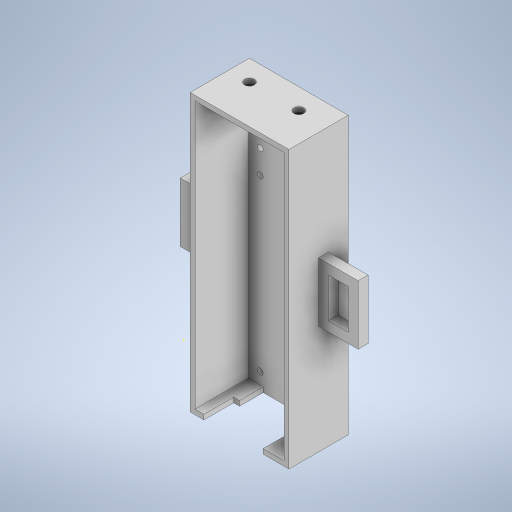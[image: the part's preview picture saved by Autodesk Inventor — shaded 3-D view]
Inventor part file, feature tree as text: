
AUTODESK INVENTOR PART (.ipt)
format: ipt  version: 2023 (Build 270158000, 158)  size: 340,480 bytes
history: native  units: mm
features: sketch x7, extrude x6, plane x1
ambient origin geometry x8: Origin, YZ Plane, XZ Plane, XY Plane, X Axis, Y Axis, Z Axis, Center Point
bodies: Solid1 (feature_tree)
feature tree (14):
  extrude  "Extrusion1"  Depth=50.0mm
  extrude  "Extrusion2"  Depth=2.5mm
  extrude  "Extrusion3"  Depth=2.5mm
  extrude  "Extrusion4"  Depth=27.0mm TaperAngle=0.0deg
  extrude  "Extrusion5"  Depth=30.0mm
  sketch  "Sketch6"  dims[d12=7.0mm d13=0.0mm]
  plane  "Work Plane1"
  extrude  "Extrusion6"  TaperAngle=0.0deg  [1 undecoded]
  sketch  "Sketch1"  dims[d0=140.0mm d1=50.0mm]
  sketch  "Sketch2"  dims[d2=30.0mm d3=0.0mm d4=2.5mm]
  sketch  "Sketch3"  dims[d5=2.5mm d6=2.5mm]
  sketch  "Sketch4"  dims[d7=2.5mm d8=27.0mm d9=0.0mm]
  sketch  "Sketch5"  dims[d10=15.0mm d11=30.0mm]
  sketch  "Sketch7"  dims[d14=25.0mm d15=10.0mm d16=3.0mm d17=27.0mm d18=0.0mm d19=8.5mm d20=8.5mm d21=8.5mm d22=8.5mm d23=3.0mm d24=3.0mm d25=8.5mm d26=8.5mm d27=8.5mm d28=8.5mm d29=3.0mm d30=3.0mm d31=3.0mm d32=3.0mm d33=12.0mm d34=12.0mm d35=33.5mm d36=33.5mm d37=27.0mm d38=0.0mm d39=5.0mm d40=5.0mm d41=25.0mm d42=14.5mm d43=10.5mm d44=10.5mm d45=27.0mm d46=0.0mm d55=-12.5mm d56=20.0mm d57=30.0mm d58=55.0mm d59=5.0mm d60=20.0mm d61=30.0mm d62=55.0mm d63=5.0mm d64=5.0mm d65=0.0mm d66=0.5mm d67=0.872665mm]
note: 1 required parameter value undecoded (feature->parameter linkage not recoverable at this tier; creation-order binding heuristic only, values carry confidence <= 0.55)
